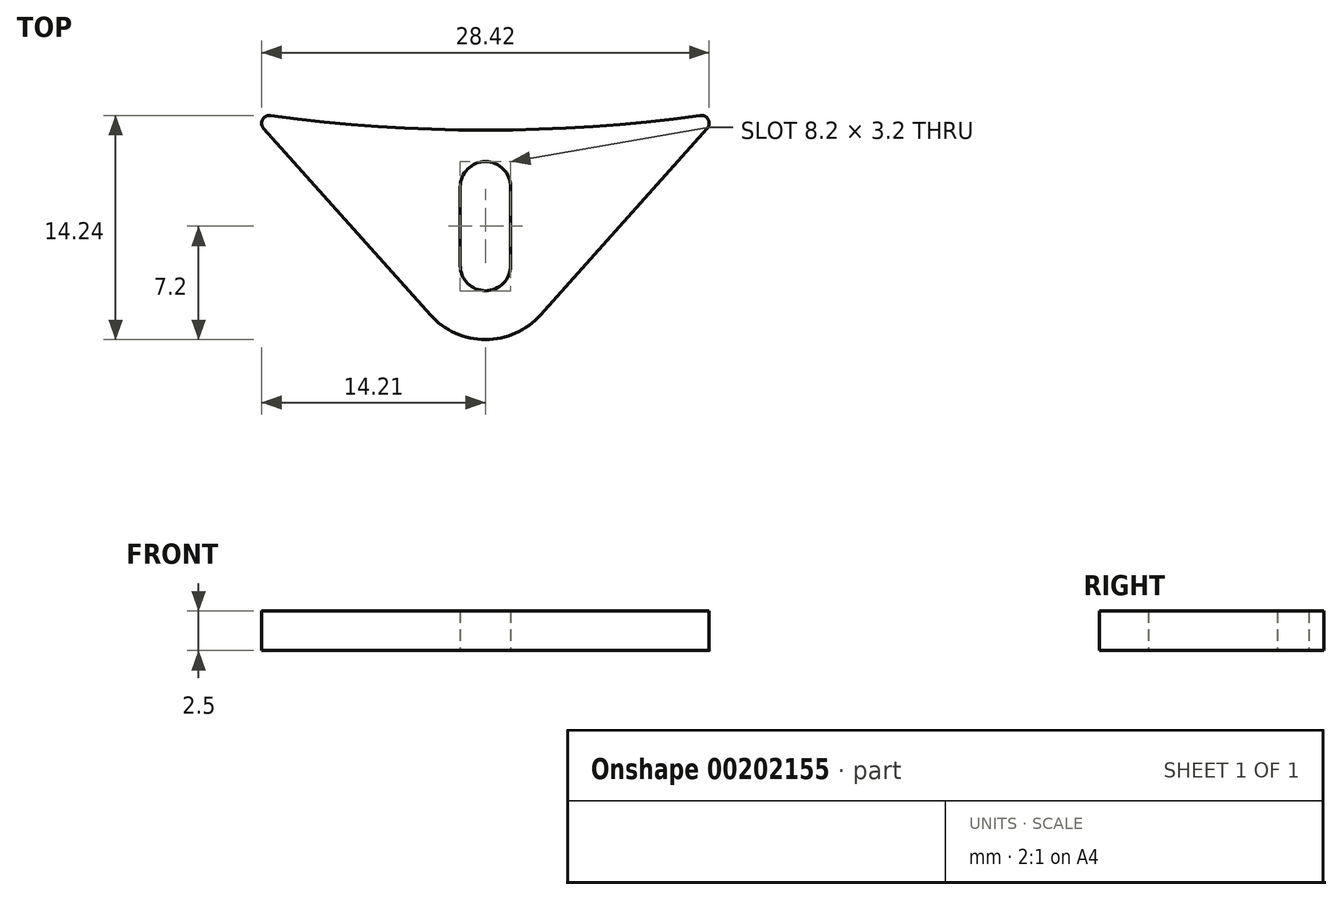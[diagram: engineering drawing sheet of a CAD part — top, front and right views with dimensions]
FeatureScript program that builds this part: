
annotation { "Feature Type Name" : "Feature", "Feature Type Description" : "" }
export const myFeature = defineFeature(function(context is Context, id is Id, definition is map)
    precondition{}
    {
        {
            var Q0;
            Q0=qCreatedBy(makeId("Top.planeOp"),FACE);
            var sketch = newSketch(context, id + "F0", { "sketchPlane" : qUnion([Q0])});
            skArc(sketch, "E0", {"start": v(-13.64, 9.53) * mm, "mid": v(0, 8.6) * mm, "end": v(13.64, 9.53) * mm});
            skLineSegment(sketch, "E1", {"start": v(-14.08, 8.7) * mm, "end": v(-3.5, -3.13) * mm});
            skLineSegment(sketch, "E2", {"start": v(3.5, -3.13) * mm, "end": v(14.08, 8.7) * mm});
            skArc(sketch, "E3", {"start": v(1.6, 5) * mm, "mid": v(0, 6.6) * mm, "end": v(-1.6, 5) * mm});
            skArc(sketch, "E4", {"start": v(-1.6, 0) * mm, "mid": v(0, -1.6) * mm, "end": v(1.6, 0) * mm});
            skLineSegment(sketch, "E5", {"start": v(-1.6, 5) * mm, "end": v(-1.6, 0) * mm});
            skLineSegment(sketch, "E6", {"start": v(1.6, 5) * mm, "end": v(1.6, 0) * mm});
            skArc(sketch, "E7", {"start": v(-3.5, -3.13) * mm, "mid": v(0, -4.7) * mm, "end": v(3.5, -3.13) * mm});
            skPoint(sketch, "E8.visualSharp", {"position": v(-15, 9.73) * mm});
            skArc(sketch, "E8.filletArc", {"start": v(-13.64, 9.53) * mm, "mid": v(-14.15, 9.27) * mm, "end": v(-14.08, 8.7) * mm});
            skPoint(sketch, "E9.visualSharp", {"position": v(15, 9.73) * mm});
            skArc(sketch, "E9.filletArc", {"start": v(14.08, 8.7) * mm, "mid": v(14.15, 9.27) * mm, "end": v(13.64, 9.53) * mm});
            skSolve(sketch);
        }
        {
            var Q0;
            Q0=makeQuery(id+"F0.imprint","IMPRINT",FACE,{"disambiguationData":[TD([[makeQuery(id+"F0.imprint","IMPRINT",EDGE,{"derivedFrom":sQuery(id+"F0.wireOp",EDGE,"E0")}),-1.0]])]});
            extrude(context, id + "F1", {"entities" : qUnion([Q0]), "depth" : 2.5 * mm});
        }
    });
